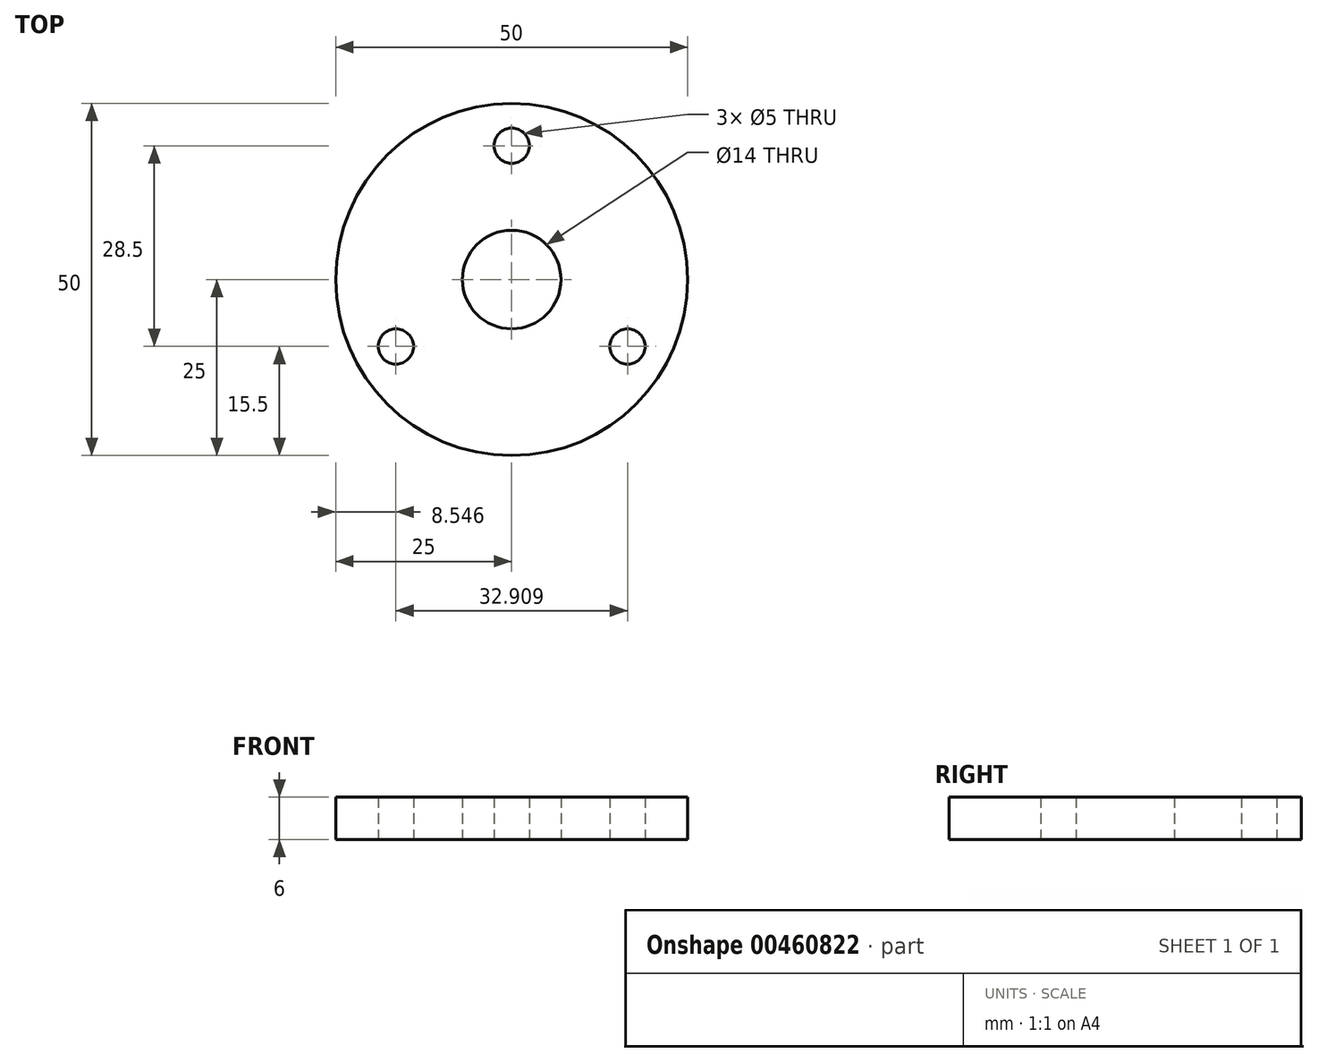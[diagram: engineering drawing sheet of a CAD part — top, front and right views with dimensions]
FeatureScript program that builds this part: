
annotation { "Feature Type Name" : "Feature", "Feature Type Description" : "" }
export const myFeature = defineFeature(function(context is Context, id is Id, definition is map)
    precondition{}
    {
        {
            var Q0;
            Q0=qCreatedBy(makeId("Top.planeOp"),FACE);
            var sketch = newSketch(context, id + "F0", { "sketchPlane" : qUnion([Q0])});
            skCircle(sketch, "E0", {"center": v(0, 0) * mm, "radius": 7 * mm});
            skCircle(sketch, "E1", {"center": v(0, 0) * mm, "radius": 25 * mm});
            skCircle(sketch, "E2", {"center": v(0, 19) * mm, "radius": 2.5 * mm});
            skCircle(sketch, "E3", {"center": v(-16.45, -9.5) * mm, "radius": 2.5 * mm});
            skCircle(sketch, "E4", {"center": v(16.45, -9.5) * mm, "radius": 2.5 * mm});
            skSolve(sketch);
        }
        {
            var Q0;
            Q0=makeQuery(id+"F0.imprint","IMPRINT",FACE,{"disambiguationData":[TD([[makeQuery(id+"F0.imprint","IMPRINT",EDGE,{"derivedFrom":sQuery(id+"F0.wireOp",EDGE,"E0")}),-1.0]])]});
            extrude(context, id + "F1", {"entities" : qUnion([Q0]), "depth" : 6 * mm});
        }
    });
